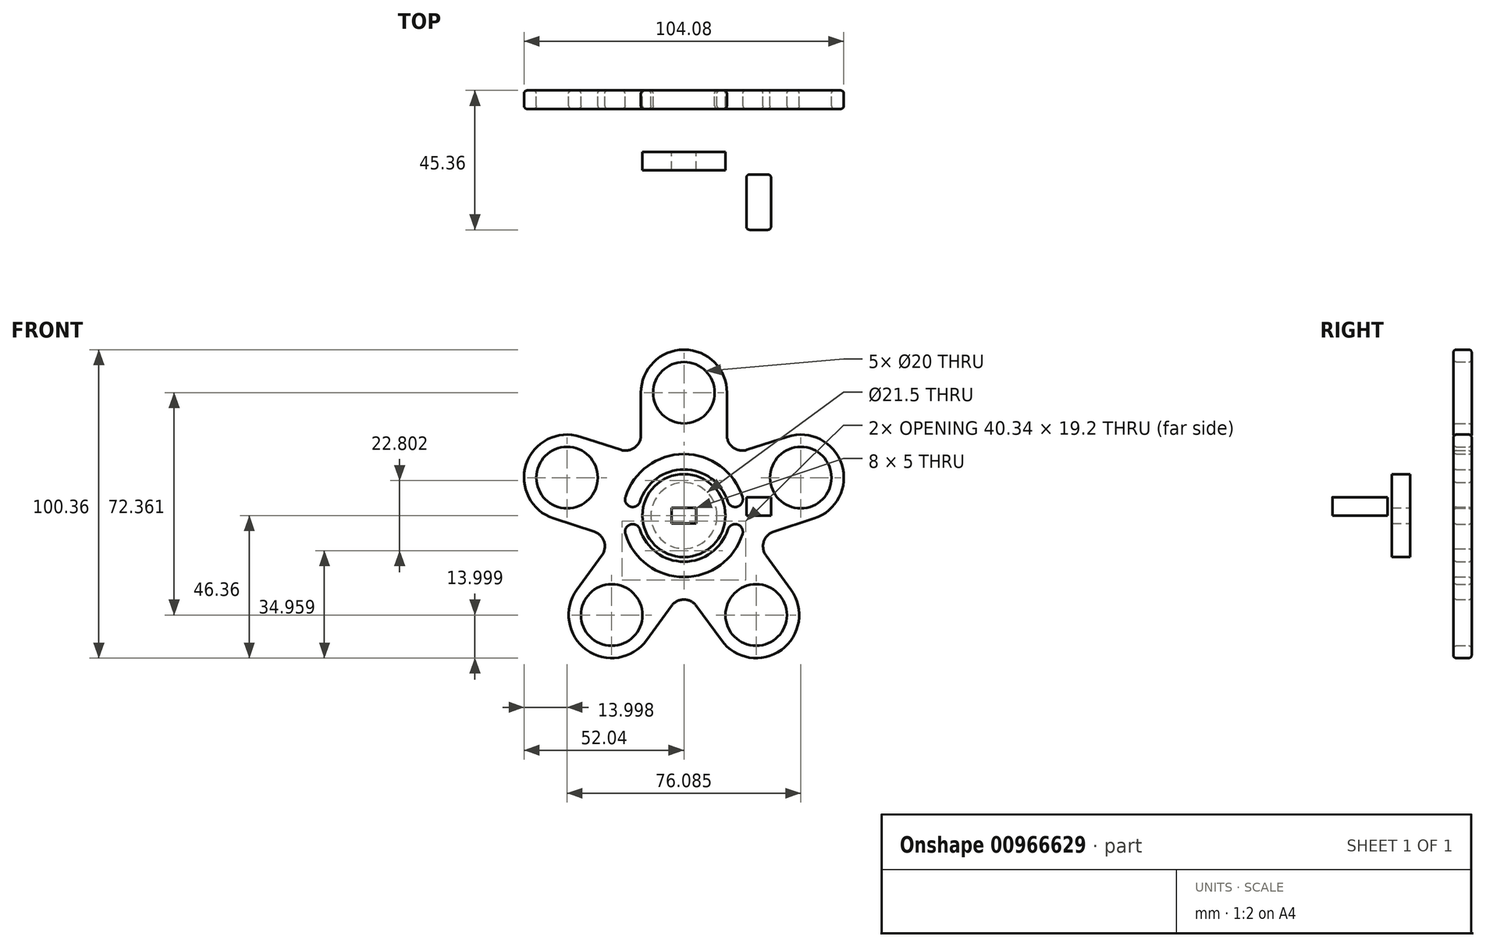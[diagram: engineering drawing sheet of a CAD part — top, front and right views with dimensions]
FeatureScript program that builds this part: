
annotation { "Feature Type Name" : "Feature", "Feature Type Description" : "" }
export const myFeature = defineFeature(function(context is Context, id is Id, definition is map)
    precondition{}
    {
        {
            var Q0;
            Q0=qCreatedBy(makeId("Front.planeOp"),FACE);
            var sketch = newSketch(context, id + "F0", { "sketchPlane" : qUnion([Q0])});
            skCircle(sketch, "E0", {"center": v(0, 0) * mm, "radius": 10.75 * mm});
            skLineSegment(sketch, "E1", {"start": v(0, 0) * mm, "end": v(0, 40) * mm, "construction": true});
            skCircle(sketch, "E2", {"center": v(0, 40) * mm, "radius": 10 * mm});
            skCircle(sketch, "E3.1.0", {"center": v(-38.04, 12.36) * mm, "radius": 10 * mm});
            skCircle(sketch, "E3.2.0", {"center": v(-23.51, -32.36) * mm, "radius": 10 * mm});
            skCircle(sketch, "E3.3.0", {"center": v(23.51, -32.36) * mm, "radius": 10 * mm});
            skCircle(sketch, "E3.4.0", {"center": v(38.04, 12.36) * mm, "radius": 10 * mm});
            skLineSegment(sketch, "E4.left", {"start": v(14, 40) * mm, "end": v(14, 26.15) * mm});
            skLineSegment(sketch, "E4.right", {"start": v(-14, 40) * mm, "end": v(-14, 26.15) * mm});
            skArc(sketch, "E5", {"start": v(14, 40) * mm, "mid": v(0, 54) * mm, "end": v(-14, 40) * mm});
            skLineSegment(sketch, "E6.1.0", {"start": v(-33.72, 25.68) * mm, "end": v(-20.55, 21.4) * mm});
            skArc(sketch, "E6.1.1", {"start": v(-33.72, 25.68) * mm, "mid": v(-51.36, 16.69) * mm, "end": v(-42.37, -0.95) * mm});
            skLineSegment(sketch, "E6.1.2", {"start": v(-42.37, -0.95) * mm, "end": v(-29.2, -5.23) * mm});
            skLineSegment(sketch, "E6.2.0", {"start": v(-34.84, -24.13) * mm, "end": v(-26.7, -12.93) * mm});
            skArc(sketch, "E6.2.1", {"start": v(-34.84, -24.13) * mm, "mid": v(-31.74, -43.69) * mm, "end": v(-12.19, -40.59) * mm});
            skLineSegment(sketch, "E6.2.2", {"start": v(-12.19, -40.59) * mm, "end": v(-4.05, -29.39) * mm});
            skLineSegment(sketch, "E6.3.0", {"start": v(12.19, -40.59) * mm, "end": v(4.05, -29.39) * mm});
            skArc(sketch, "E6.3.1", {"start": v(12.19, -40.59) * mm, "mid": v(31.74, -43.69) * mm, "end": v(34.84, -24.13) * mm});
            skLineSegment(sketch, "E6.3.2", {"start": v(34.84, -24.13) * mm, "end": v(26.7, -12.93) * mm});
            skLineSegment(sketch, "E6.4.0", {"start": v(42.37, -0.95) * mm, "end": v(29.2, -5.23) * mm});
            skArc(sketch, "E6.4.1", {"start": v(42.37, -0.95) * mm, "mid": v(51.36, 16.69) * mm, "end": v(33.72, 25.68) * mm});
            skLineSegment(sketch, "E6.4.2", {"start": v(33.72, 25.68) * mm, "end": v(20.55, 21.4) * mm});
            skPoint(sketch, "E7.orphan", {"position": v(-17.5, -0.27) * mm});
            skPoint(sketch, "E8.orphan", {"position": v(-14.31, -10.07) * mm});
            skPoint(sketch, "E9.orphan", {"position": v(-5.15, -16.72) * mm});
            skPoint(sketch, "E10.orphan", {"position": v(5.15, -16.72) * mm});
            skPoint(sketch, "E11.orphan", {"position": v(14.31, -10.07) * mm});
            skPoint(sketch, "E12.orphan", {"position": v(17.5, -0.27) * mm});
            skArc(sketch, "E13.filletArc", {"start": v(-20.55, 21.4) * mm, "mid": v(-16.06, 22.1) * mm, "end": v(-14, 26.15) * mm});
            skArc(sketch, "E14.filletArc", {"start": v(14, 26.15) * mm, "mid": v(16.06, 22.1) * mm, "end": v(20.55, 21.4) * mm});
            skPoint(sketch, "E15.visualSharp", {"position": v(22.65, -7.36) * mm});
            skArc(sketch, "E15.filletArc", {"start": v(29.2, -5.23) * mm, "mid": v(25.99, -8.44) * mm, "end": v(26.7, -12.93) * mm});
            skPoint(sketch, "E16.visualSharp", {"position": v(0, -23.82) * mm});
            skArc(sketch, "E16.filletArc", {"start": v(4.05, -29.39) * mm, "mid": v(0, -27.32) * mm, "end": v(-4.05, -29.39) * mm});
            skPoint(sketch, "E17.visualSharp", {"position": v(-22.65, -7.36) * mm});
            skArc(sketch, "E17.filletArc", {"start": v(-26.7, -12.93) * mm, "mid": v(-25.99, -8.44) * mm, "end": v(-29.2, -5.23) * mm});
            skArc(sketch, "E18", {"start": v(-16.68, -5.29) * mm, "mid": v(0, -17.5) * mm, "end": v(16.68, -5.29) * mm});
            skArc(sketch, "E19.trimOffspring", {"start": v(16.68, 5.29) * mm, "mid": v(0, 17.5) * mm, "end": v(-16.68, 5.29) * mm});
            skArc(sketch, "E20.0.startCap", {"start": v(19.06, 6.05) * mm, "mid": v(17.44, 2.9) * mm, "end": v(14.3, 4.53) * mm});
            skArc(sketch, "E20.0.endCap", {"start": v(-14.3, 4.53) * mm, "mid": v(-17.44, 2.9) * mm, "end": v(-19.06, 6.05) * mm});
            skArc(sketch, "E20.0.left", {"start": v(14.3, 4.53) * mm, "mid": v(0, 15) * mm, "end": v(-14.3, 4.53) * mm});
            skArc(sketch, "E20.0.right", {"start": v(19.06, 6.05) * mm, "mid": v(0, 20) * mm, "end": v(-19.06, 6.05) * mm});
            skArc(sketch, "E21.0.startCap", {"start": v(-19.06, -6.05) * mm, "mid": v(-17.44, -2.9) * mm, "end": v(-14.3, -4.53) * mm});
            skArc(sketch, "E21.0.endCap", {"start": v(14.3, -4.53) * mm, "mid": v(17.44, -2.9) * mm, "end": v(19.06, -6.05) * mm});
            skArc(sketch, "E21.0.left", {"start": v(-14.3, -4.53) * mm, "mid": v(0, -15) * mm, "end": v(14.3, -4.53) * mm});
            skArc(sketch, "E21.0.right", {"start": v(-19.06, -6.05) * mm, "mid": v(0, -20) * mm, "end": v(19.06, -6.05) * mm});
            skSolve(sketch);
        }
        {
            var Q0;
            Q0=makeQuery(id+"F0.imprint","IMPRINT",FACE,{"disambiguationData":[TD([[makeQuery(id+"F0.imprint","IMPRINT",EDGE,{"derivedFrom":sQuery(id+"F0.wireOp",EDGE,"E0")}),-1.0]])]});
            extrude(context, id + "F1", {"entities" : qUnion([Q0]), "depth" : 6 * mm, "offsetDistance" : 25 * mm});
        }
        {
            var Q0;
            Q0=makeQuery(id+"F1.opExtrude","CAP_FACE",FACE,{"disambiguationData":[OSD([sQuery(id+"F0.wireOp",EDGE,"E0"),sQuery(id+"F0.wireOp",EDGE,"E2"),sQuery(id+"F0.wireOp",EDGE,"E3.1.0"),sQuery(id+"F0.wireOp",EDGE,"E3.2.0"),sQuery(id+"F0.wireOp",EDGE,"E3.3.0"),sQuery(id+"F0.wireOp",EDGE,"E3.4.0"),sQuery(id+"F0.wireOp",EDGE,"E4.left"),sQuery(id+"F0.wireOp",EDGE,"E4.right"),sQuery(id+"F0.wireOp",EDGE,"E5"),sQuery(id+"F0.wireOp",EDGE,"E6.1.0"),sQuery(id+"F0.wireOp",EDGE,"E6.1.1"),sQuery(id+"F0.wireOp",EDGE,"E6.1.2"),sQuery(id+"F0.wireOp",EDGE,"E6.2.0"),sQuery(id+"F0.wireOp",EDGE,"E6.2.1"),sQuery(id+"F0.wireOp",EDGE,"E6.2.2"),sQuery(id+"F0.wireOp",EDGE,"E6.3.0"),sQuery(id+"F0.wireOp",EDGE,"E6.3.1"),sQuery(id+"F0.wireOp",EDGE,"E6.3.2"),sQuery(id+"F0.wireOp",EDGE,"E6.4.0"),sQuery(id+"F0.wireOp",EDGE,"E6.4.1"),sQuery(id+"F0.wireOp",EDGE,"E6.4.2"),sQuery(id+"F0.wireOp",EDGE,"E13.filletArc"),sQuery(id+"F0.wireOp",EDGE,"E14.filletArc"),sQuery(id+"F0.wireOp",EDGE,"E15.filletArc"),sQuery(id+"F0.wireOp",EDGE,"E16.filletArc"),sQuery(id+"F0.wireOp",EDGE,"E17.filletArc")])],"isStart":false});
            var Q1;
            Q1=makeQuery(id+"F1.opExtrude","CAP_FACE",FACE,{"disambiguationData":[OSD([sQuery(id+"F0.wireOp",EDGE,"E0"),sQuery(id+"F0.wireOp",EDGE,"E2"),sQuery(id+"F0.wireOp",EDGE,"E3.1.0"),sQuery(id+"F0.wireOp",EDGE,"E3.2.0"),sQuery(id+"F0.wireOp",EDGE,"E3.3.0"),sQuery(id+"F0.wireOp",EDGE,"E3.4.0"),sQuery(id+"F0.wireOp",EDGE,"E4.left"),sQuery(id+"F0.wireOp",EDGE,"E4.right"),sQuery(id+"F0.wireOp",EDGE,"E5"),sQuery(id+"F0.wireOp",EDGE,"E6.1.0"),sQuery(id+"F0.wireOp",EDGE,"E6.1.1"),sQuery(id+"F0.wireOp",EDGE,"E6.1.2"),sQuery(id+"F0.wireOp",EDGE,"E6.2.0"),sQuery(id+"F0.wireOp",EDGE,"E6.2.1"),sQuery(id+"F0.wireOp",EDGE,"E6.2.2"),sQuery(id+"F0.wireOp",EDGE,"E6.3.0"),sQuery(id+"F0.wireOp",EDGE,"E6.3.1"),sQuery(id+"F0.wireOp",EDGE,"E6.3.2"),sQuery(id+"F0.wireOp",EDGE,"E6.4.0"),sQuery(id+"F0.wireOp",EDGE,"E6.4.1"),sQuery(id+"F0.wireOp",EDGE,"E6.4.2"),sQuery(id+"F0.wireOp",EDGE,"E13.filletArc"),sQuery(id+"F0.wireOp",EDGE,"E14.filletArc"),sQuery(id+"F0.wireOp",EDGE,"E15.filletArc"),sQuery(id+"F0.wireOp",EDGE,"E16.filletArc"),sQuery(id+"F0.wireOp",EDGE,"E17.filletArc")])],"isStart":true});
            fillet(context, id + "F2", {"entities" : qUnion([Q0, Q1]), "radius" : 1 * mm, "tangentPropagation" : true, "allowEdgeOverflow" : false});
        }
        {
            var Q0;
            Q0=qCreatedBy(makeId("Top.planeOp"),FACE);
            var sketch = newSketch(context, id + "F3", { "sketchPlane" : qUnion([Q0])});
            skLineSegment(sketch, "E22.bottom", {"start": v(21.35, -27.36) * mm, "end": v(27.35, -27.36) * mm});
            skLineSegment(sketch, "E22.top", {"start": v(21.35, -45.36) * mm, "end": v(27.35, -45.36) * mm});
            skLineSegment(sketch, "E22.left", {"start": v(20.35, -28.36) * mm, "end": v(20.35, -44.36) * mm});
            skLineSegment(sketch, "E22.right", {"start": v(28.35, -28.36) * mm, "end": v(28.35, -44.36) * mm});
            skPoint(sketch, "E22.middle", {"position": v(24.35, -36.36) * mm});
            skPoint(sketch, "E23.visualSharp", {"position": v(20.35, -45.36) * mm});
            skArc(sketch, "E23.filletArc", {"start": v(20.35, -44.36) * mm, "mid": v(20.64, -45.06) * mm, "end": v(21.35, -45.36) * mm});
            skPoint(sketch, "E24.visualSharp", {"position": v(28.35, -45.36) * mm});
            skArc(sketch, "E24.filletArc", {"start": v(27.35, -45.36) * mm, "mid": v(28.05, -45.06) * mm, "end": v(28.35, -44.36) * mm});
            skPoint(sketch, "E25.visualSharp", {"position": v(28.35, -27.36) * mm});
            skArc(sketch, "E25.filletArc", {"start": v(28.35, -28.36) * mm, "mid": v(28.05, -27.65) * mm, "end": v(27.35, -27.36) * mm});
            skPoint(sketch, "E26.visualSharp", {"position": v(20.35, -27.36) * mm});
            skArc(sketch, "E26.filletArc", {"start": v(21.35, -27.36) * mm, "mid": v(20.64, -27.65) * mm, "end": v(20.35, -28.36) * mm});
            skSolve(sketch);
        }
        {
            var Q0;
            Q0=makeQuery(id+"F3.imprint","IMPRINT",FACE,{"disambiguationData":[TD([[makeQuery(id+"F3.imprint","IMPRINT",EDGE,{"derivedFrom":sQuery(id+"F3.wireOp",EDGE,"E22.bottom")}),-1.0]])]});
            extrude(context, id + "F4", {"entities" : qUnion([Q0]), "depth" : 6 * mm, "offsetDistance" : 25 * mm});
        }
        {
            var Q0;
            Q0=qCreatedBy(makeId("Front.planeOp"),FACE);
            var sketch = newSketch(context, id + "F5", { "sketchPlane" : qUnion([Q0])});
            skCircle(sketch, "E27", {"center": v(0, 0) * mm, "radius": 13.5 * mm});
            skLineSegment(sketch, "E28.bottom", {"start": v(4, -2.5) * mm, "end": v(-4, -2.5) * mm});
            skLineSegment(sketch, "E28.top", {"start": v(4, 2.5) * mm, "end": v(-4, 2.5) * mm});
            skLineSegment(sketch, "E28.left", {"start": v(4, -2.5) * mm, "end": v(4, 2.5) * mm});
            skLineSegment(sketch, "E28.right", {"start": v(-4, -2.5) * mm, "end": v(-4, 2.5) * mm});
            skSolve(sketch);
        }
        {
            var Q0;
            Q0=qSketchRegion(id+"F5",true);
            extrude(context, id + "F6", {"entities" : qUnion([Q0]), "depth" : 26 * mm, "offsetDistance" : 25 * mm, "hasSecondDirection" : true, "secondDirectionOppositeDirection" : false, "secondDirectionDepth" : 20 * mm});
        }
    });
